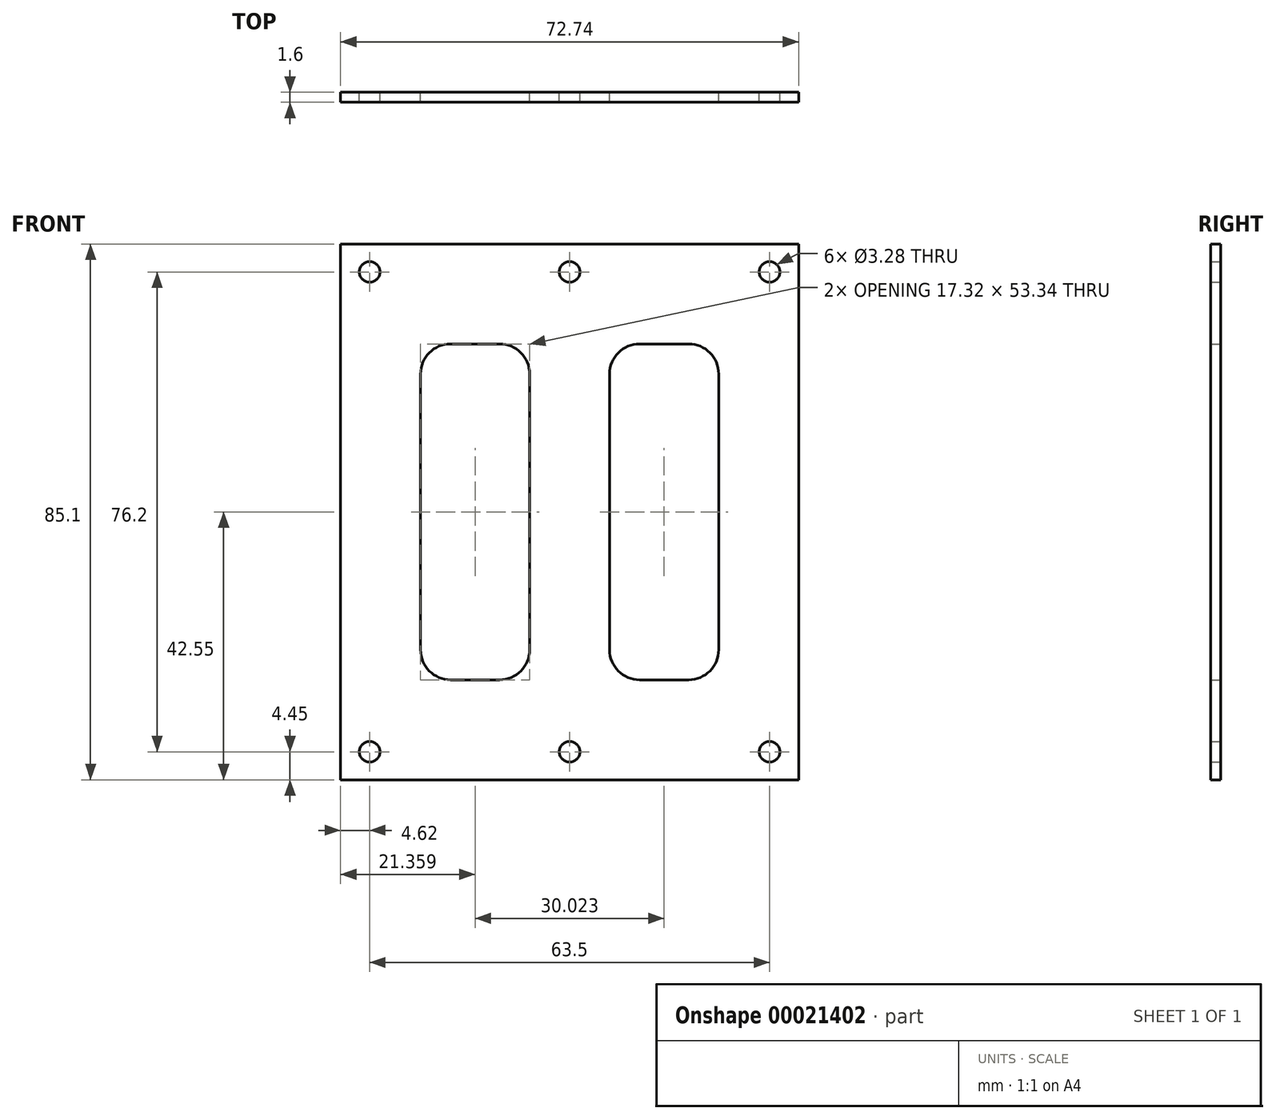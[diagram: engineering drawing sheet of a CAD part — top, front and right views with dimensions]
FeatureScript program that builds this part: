
annotation { "Feature Type Name" : "Feature", "Feature Type Description" : "" }
export const myFeature = defineFeature(function(context is Context, id is Id, definition is map)
    precondition{}
    {
        {
            var Q0;
            Q0=qCreatedBy(makeId("Front.planeOp"),FACE);
            var sketch = newSketch(context, id + "F0", { "sketchPlane" : qUnion([Q0])});
            skLineSegment(sketch, "E0.rect.bottom", {"start": v(-36.37, 42.55) * mm, "end": v(36.37, 42.55) * mm});
            skLineSegment(sketch, "E0.rect.top", {"start": v(-36.37, -42.55) * mm, "end": v(36.37, -42.55) * mm});
            skLineSegment(sketch, "E0.rect.left", {"start": v(-36.37, 42.55) * mm, "end": v(-36.37, -42.55) * mm});
            skLineSegment(sketch, "E0.rect.right", {"start": v(36.37, 42.55) * mm, "end": v(36.37, -42.55) * mm});
            skPoint(sketch, "E0.rect.middle", {"position": v(0, 0) * mm});
            skLineSegment(sketch, "E1.bottom", {"start": v(-23.67, 26.67) * mm, "end": v(-6.35, 26.67) * mm});
            skLineSegment(sketch, "E1.top", {"start": v(-23.67, -26.67) * mm, "end": v(-6.35, -26.67) * mm});
            skLineSegment(sketch, "E1.left", {"start": v(-23.67, 26.67) * mm, "end": v(-23.67, -26.67) * mm});
            skLineSegment(sketch, "E1.right", {"start": v(-6.35, 26.67) * mm, "end": v(-6.35, -26.67) * mm});
            skLineSegment(sketch, "E2.bottom", {"start": v(6.35, 26.67) * mm, "end": v(23.67, 26.67) * mm});
            skLineSegment(sketch, "E2.top", {"start": v(6.35, -26.67) * mm, "end": v(23.67, -26.67) * mm});
            skLineSegment(sketch, "E2.left", {"start": v(6.35, 26.67) * mm, "end": v(6.35, -26.67) * mm});
            skLineSegment(sketch, "E2.right", {"start": v(23.67, 26.67) * mm, "end": v(23.67, -26.67) * mm});
            skLineSegment(sketch, "E3", {"start": v(0, 0) * mm, "end": v(0, 64.2) * mm});
            skLineSegment(sketch, "E4", {"start": v(0, 0) * mm, "end": v(59.73, 0) * mm});
            skSolve(sketch);
        }
        {
            var Q0;
            {var subQ12=sQuery(id+"F0.wireOp",EDGE,"E0.rect.top");Q0=makeQuery(id+"F0.imprint","IMPRINT",FACE,{"disambiguationData":[TD([[makeQuery(id+"F0.imprint","IMPRINT",EDGE,{"derivedFrom":subQ12}),1.0]])]});}
            var Q1;
            {var subQ7=sQuery(id+"F0.wireOp",EDGE,"E2.bottom");Q1=makeQuery(id+"F0.imprint","IMPRINT",FACE,{"disambiguationData":[TD([[makeQuery(id+"F0.imprint","IMPRINT",EDGE,{"derivedFrom":subQ7}),1.0]])]});}
            extrude(context, id + "F1", {"entities" : qUnion([Q0, Q1]), "depth" : 1.6 * mm});
        }
        {
            var Q0;
            Q0=makeQuery(id+"F1.opExtrude","SWEPT_EDGE",EDGE,{"disambiguationData":[OSD([sQuery(id+"F0.wireOp",EDGE,"E2.bottom"),sQuery(id+"F0.wireOp",EDGE,"E2.left")])]});
            var Q1;
            Q1=makeQuery(id+"F1.opExtrude","SWEPT_EDGE",EDGE,{"disambiguationData":[OSD([sQuery(id+"F0.wireOp",EDGE,"E2.bottom"),sQuery(id+"F0.wireOp",EDGE,"E2.right")])]});
            var Q2;
            Q2=makeQuery(id+"F1.opExtrude","SWEPT_EDGE",EDGE,{"disambiguationData":[OSD([sQuery(id+"F0.wireOp",EDGE,"E2.top"),sQuery(id+"F0.wireOp",EDGE,"E2.left")])]});
            var Q3;
            Q3=makeQuery(id+"F1.opExtrude","SWEPT_EDGE",EDGE,{"disambiguationData":[OSD([sQuery(id+"F0.wireOp",EDGE,"E2.top"),sQuery(id+"F0.wireOp",EDGE,"E2.right")])]});
            var Q4;
            Q4=makeQuery(id+"F1.opExtrude","SWEPT_EDGE",EDGE,{"disambiguationData":[OSD([sQuery(id+"F0.wireOp",EDGE,"E1.bottom"),sQuery(id+"F0.wireOp",EDGE,"E1.right")])]});
            var Q5;
            Q5=makeQuery(id+"F1.opExtrude","SWEPT_EDGE",EDGE,{"disambiguationData":[OSD([sQuery(id+"F0.wireOp",EDGE,"E1.top"),sQuery(id+"F0.wireOp",EDGE,"E1.right")])]});
            var Q6;
            Q6=makeQuery(id+"F1.opExtrude","SWEPT_EDGE",EDGE,{"disambiguationData":[OSD([sQuery(id+"F0.wireOp",EDGE,"E1.bottom"),sQuery(id+"F0.wireOp",EDGE,"E1.left")])]});
            var Q7;
            Q7=makeQuery(id+"F1.opExtrude","SWEPT_EDGE",EDGE,{"disambiguationData":[OSD([sQuery(id+"F0.wireOp",EDGE,"E1.top"),sQuery(id+"F0.wireOp",EDGE,"E1.left")])]});
            fillet(context, id + "F2", {"entities" : qUnion([Q0, Q1, Q2, Q3, Q4, Q5, Q6, Q7]), "radius" : 4.78 * mm, "tangentPropagation" : true, "allowEdgeOverflow" : false});
        }
        {
            var Q0;
            Q0=qCreatedBy(makeId("Front.planeOp"),FACE);
            var sketch = newSketch(context, id + "F3", { "sketchPlane" : qUnion([Q0])});
            skLineSegment(sketch, "E5.rect.bottom", {"start": v(-31.75, -38.1) * mm, "end": v(31.75, -38.1) * mm});
            skLineSegment(sketch, "E5.rect.top", {"start": v(-31.75, 38.1) * mm, "end": v(31.75, 38.1) * mm});
            skLineSegment(sketch, "E5.rect.left", {"start": v(-31.75, -38.1) * mm, "end": v(-31.75, 38.1) * mm});
            skLineSegment(sketch, "E5.rect.right", {"start": v(31.75, -38.1) * mm, "end": v(31.75, 38.1) * mm});
            skPoint(sketch, "E5.rect.middle", {"position": v(0, 0) * mm});
            skLineSegment(sketch, "E6", {"start": v(0, 0) * mm, "end": v(0, 38.1) * mm});
            skLineSegment(sketch, "E7", {"start": v(0, 0) * mm, "end": v(0, -38.1) * mm});
            skSolve(sketch);
        }
        {
            var Q0;
            Q0=sQuery(id+"F3.wireOp",VERTEX,"E5.rect.left.end");
            var Q1;
            Q1=sQuery(id+"F3.wireOp",VERTEX,"E6.end");
            var Q2;
            Q2=sQuery(id+"F3.wireOp",VERTEX,"E5.rect.right.end");
            var Q3;
            Q3=sQuery(id+"F3.wireOp",VERTEX,"E5.rect.right.start");
            var Q4;
            Q4=sQuery(id+"F3.wireOp",VERTEX,"E7.end");
            var Q5;
            Q5=sQuery(id+"F3.wireOp",VERTEX,"E5.rect.bottom.start");
            var Q6;
            Q6=makeQuery(id+"F1.opExtrude","SWEPT_BODY",BODY,{"disambiguationData":[OSD([sQuery(id+"F0.wireOp",EDGE,"E0.rect.bottom"),sQuery(id+"F0.wireOp",EDGE,"E0.rect.top"),sQuery(id+"F0.wireOp",EDGE,"E0.rect.left"),sQuery(id+"F0.wireOp",EDGE,"E0.rect.right"),sQuery(id+"F0.wireOp",EDGE,"E1.bottom"),sQuery(id+"F0.wireOp",EDGE,"E1.top"),sQuery(id+"F0.wireOp",EDGE,"E1.left"),sQuery(id+"F0.wireOp",EDGE,"E1.right"),sQuery(id+"F0.wireOp",EDGE,"E2.bottom"),sQuery(id+"F0.wireOp",EDGE,"E2.top"),sQuery(id+"F0.wireOp",EDGE,"E2.left"),sQuery(id+"F0.wireOp",EDGE,"E2.right")])]});
            hole(context, id + "F4", {"style" : HoleStyle.SIMPLE, "holeDiameter" : 3.28 * mm, "endStyle" : HoleEndStyle.THROUGH, "oppositeDirection" : true, "locations" : qUnion([Q0, Q1, Q2, Q3, Q4, Q5]), "scope" : qUnion([Q6])});
        }
    });
